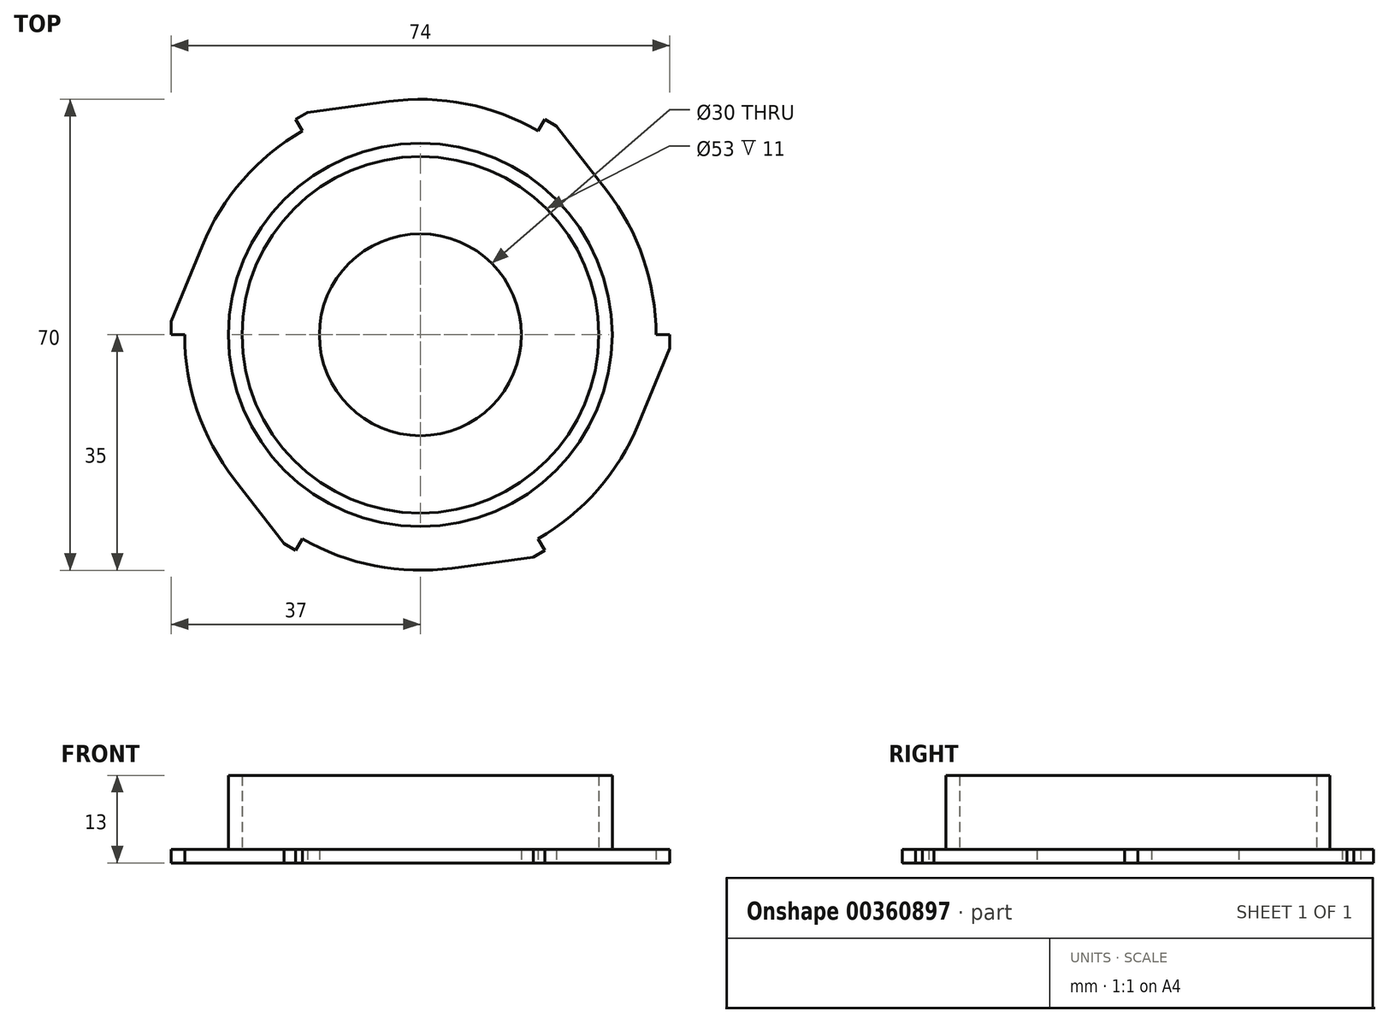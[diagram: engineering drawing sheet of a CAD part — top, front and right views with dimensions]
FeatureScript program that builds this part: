
annotation { "Feature Type Name" : "Feature", "Feature Type Description" : "" }
export const myFeature = defineFeature(function(context is Context, id is Id, definition is map)
    precondition{}
    {
        {
            var Q0;
            Q0=qCreatedBy(makeId("Front.planeOp"),FACE);
            var sketch = newSketch(context, id + "F0", { "sketchPlane" : qUnion([Q0])});
            skLineSegment(sketch, "E0", {"start": v(0, 0) * mm, "end": v(35, 0) * mm});
            skLineSegment(sketch, "E1", {"start": v(0, 0) * mm, "end": v(0, 14.67) * mm});
            skLineSegment(sketch, "E2", {"start": v(0, 0) * mm, "end": v(28.5, 0) * mm});
            skLineSegment(sketch, "E3", {"start": v(0, 0) * mm, "end": v(15, 0) * mm});
            skLineSegment(sketch, "E4", {"start": v(28.5, 2) * mm, "end": v(28.5, 13) * mm});
            skLineSegment(sketch, "E5.0", {"start": v(15, 2) * mm, "end": v(26.5, 2) * mm});
            skLineSegment(sketch, "E6.0", {"start": v(26.5, 2) * mm, "end": v(26.5, 13) * mm});
            skLineSegment(sketch, "E7", {"start": v(35, 2) * mm, "end": v(35, 0) * mm});
            skLineSegment(sketch, "E8", {"start": v(26.5, 13) * mm, "end": v(28.5, 13) * mm});
            skLineSegment(sketch, "E9.trimOffspring", {"start": v(28.5, 2) * mm, "end": v(35, 2) * mm});
            skLineSegment(sketch, "E10", {"start": v(15, 0) * mm, "end": v(15, 2) * mm});
            skSolve(sketch);
        }
        {
            var Q0;
            Q0 = qSketchRegion(id + "F0", true);
            var Q1;
            Q1=sQuery(id+"F0.wireOp",EDGE,"E1");
            revolve(context, id + "F1", {"entities" : qUnion([Q0]), "axis" : qUnion([Q1]), "revolveType" : RevolveType.FULL, "surfaceOperationType" : NewSurfaceOperationType.NEW});
        }
        {
            var Q0;
            Q0=qCreatedBy(makeId("Top.planeOp"),FACE);
            var sketch = newSketch(context, id + "F2", { "sketchPlane" : qUnion([Q0])});
            skCircle(sketch, "E11", {"center": v(0, 0) * mm, "radius": 35 * mm});
            skLineSegment(sketch, "E12", {"start": v(35, 0) * mm, "end": v(37, 0) * mm});
            skLineSegment(sketch, "E13", {"start": v(37, 0) * mm, "end": v(37, -2) * mm});
            skLineSegment(sketch, "E14", {"start": v(37, -2) * mm, "end": v(32.4, -13.26) * mm});
            skLineSegment(sketch, "E15.1.0", {"start": v(17.5, 30.31) * mm, "end": v(18.5, 32.04) * mm});
            skLineSegment(sketch, "E15.1.1", {"start": v(18.5, 32.04) * mm, "end": v(20.23, 31.04) * mm});
            skLineSegment(sketch, "E15.1.2", {"start": v(20.23, 31.04) * mm, "end": v(27.68, 21.42) * mm});
            skLineSegment(sketch, "E15.2.0", {"start": v(-17.5, 30.31) * mm, "end": v(-18.5, 32.04) * mm});
            skLineSegment(sketch, "E15.2.1", {"start": v(-18.5, 32.04) * mm, "end": v(-16.77, 33.04) * mm});
            skLineSegment(sketch, "E15.2.2", {"start": v(-16.77, 33.04) * mm, "end": v(-4.71, 34.68) * mm});
            skLineSegment(sketch, "E15.3.0", {"start": v(-35, 0) * mm, "end": v(-37, 0) * mm});
            skLineSegment(sketch, "E15.3.1", {"start": v(-37, 0) * mm, "end": v(-37, 2) * mm});
            skLineSegment(sketch, "E15.3.2", {"start": v(-37, 2) * mm, "end": v(-32.4, 13.26) * mm});
            skLineSegment(sketch, "E15.4.0", {"start": v(-17.5, -30.31) * mm, "end": v(-18.5, -32.04) * mm});
            skLineSegment(sketch, "E15.4.1", {"start": v(-18.5, -32.04) * mm, "end": v(-20.23, -31.04) * mm});
            skLineSegment(sketch, "E15.4.2", {"start": v(-20.23, -31.04) * mm, "end": v(-27.68, -21.42) * mm});
            skLineSegment(sketch, "E15.5.0", {"start": v(17.5, -30.31) * mm, "end": v(18.5, -32.04) * mm});
            skLineSegment(sketch, "E15.5.1", {"start": v(18.5, -32.04) * mm, "end": v(16.77, -33.04) * mm});
            skLineSegment(sketch, "E15.5.2", {"start": v(16.77, -33.04) * mm, "end": v(4.71, -34.68) * mm});
            skSolve(sketch);
        }
        {
            var Q0;
            {var subQ0=sQuery(id+"F2.wireOp",EDGE,"E12");Q0=makeQuery(id+"F2.imprint","IMPRINT",FACE,{"disambiguationData":[TD([[makeQuery(id+"F2.imprint","IMPRINT",EDGE,{"derivedFrom":subQ0}),-1.0]])]});}
            var Q1;
            {var subQ0=sQuery(id+"F2.wireOp",EDGE,"E15.5.0");Q1=makeQuery(id+"F2.imprint","IMPRINT",FACE,{"disambiguationData":[TD([[makeQuery(id+"F2.imprint","IMPRINT",EDGE,{"derivedFrom":subQ0}),-1.0]])]});}
            var Q2;
            {var subQ0=sQuery(id+"F2.wireOp",EDGE,"E15.1.0");Q2=makeQuery(id+"F2.imprint","IMPRINT",FACE,{"disambiguationData":[TD([[makeQuery(id+"F2.imprint","IMPRINT",EDGE,{"derivedFrom":subQ0}),-1.0]])]});}
            var Q3;
            {var subQ0=sQuery(id+"F2.wireOp",EDGE,"E15.2.0");Q3=makeQuery(id+"F2.imprint","IMPRINT",FACE,{"disambiguationData":[TD([[makeQuery(id+"F2.imprint","IMPRINT",EDGE,{"derivedFrom":subQ0}),-1.0]])]});}
            var Q4;
            {var subQ0=sQuery(id+"F2.wireOp",EDGE,"E15.3.0");Q4=makeQuery(id+"F2.imprint","IMPRINT",FACE,{"disambiguationData":[TD([[makeQuery(id+"F2.imprint","IMPRINT",EDGE,{"derivedFrom":subQ0}),-1.0]])]});}
            var Q5;
            {var subQ0=sQuery(id+"F2.wireOp",EDGE,"E15.4.0");Q5=makeQuery(id+"F2.imprint","IMPRINT",FACE,{"disambiguationData":[TD([[makeQuery(id+"F2.imprint","IMPRINT",EDGE,{"derivedFrom":subQ0}),-1.0]])]});}
            extrude(context, id + "F3", {"entities" : qUnion([Q0, Q1, Q2, Q3, Q4, Q5]), "operationType" : NewBodyOperationType.ADD, "depth" : 2 * mm, "offsetDistance" : 25 * mm});
        }
    });
